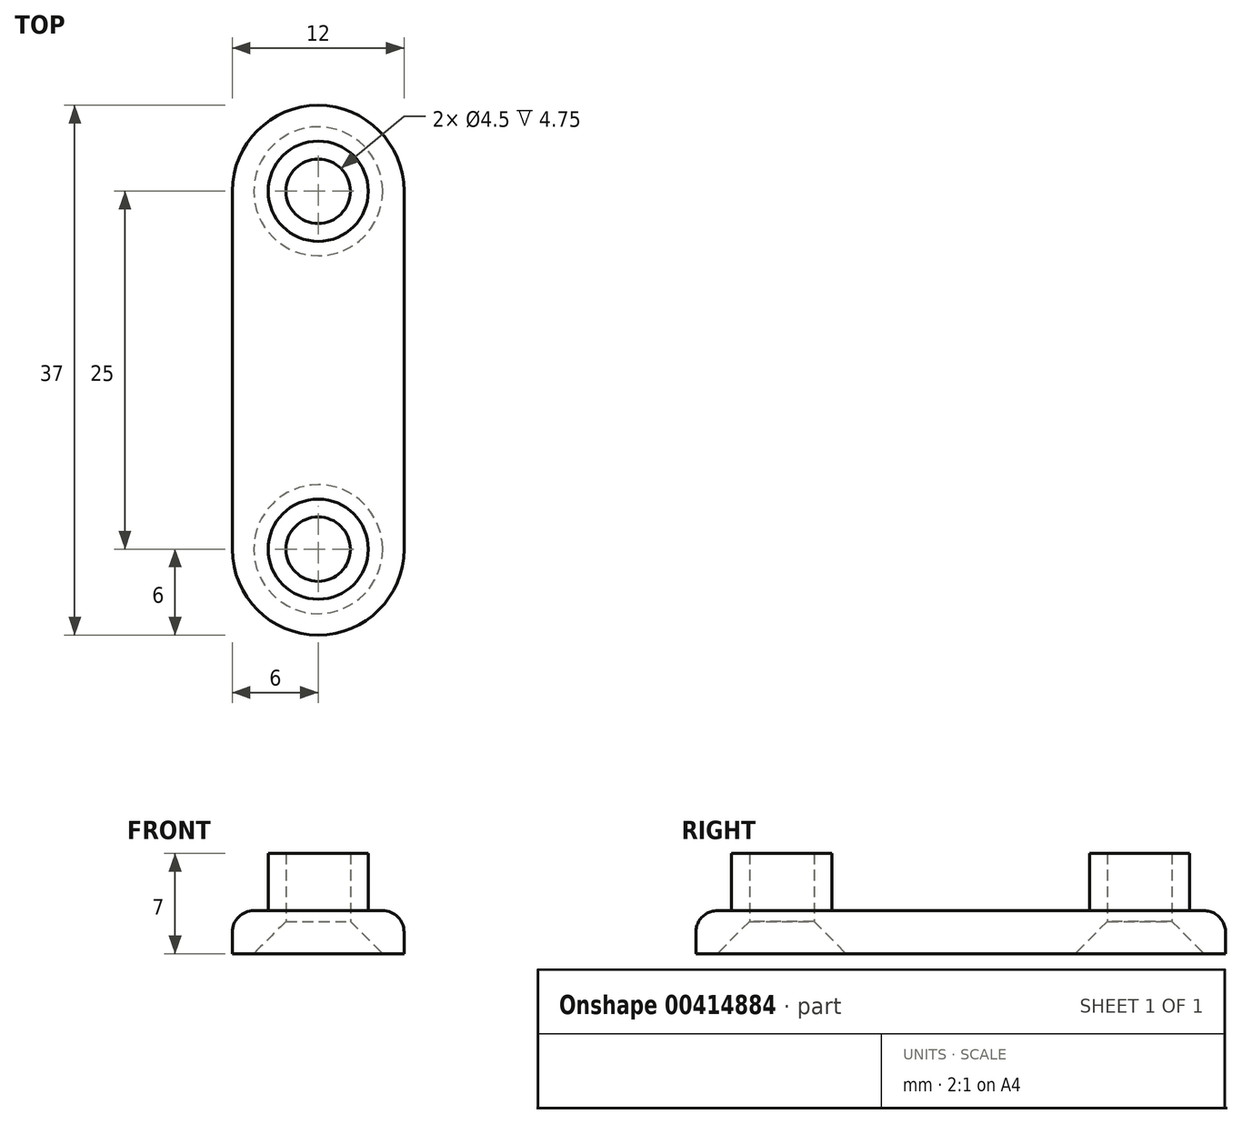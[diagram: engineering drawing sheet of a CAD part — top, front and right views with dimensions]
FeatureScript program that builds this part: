
annotation { "Feature Type Name" : "Feature", "Feature Type Description" : "" }
export const myFeature = defineFeature(function(context is Context, id is Id, definition is map)
    precondition{}
    {
        {
            var Q0;
            Q0=qCreatedBy(makeId("Top.planeOp"),FACE);
            var sketch = newSketch(context, id + "F0", { "sketchPlane" : qUnion([Q0])});
            skLineSegment(sketch, "E0", {"start": v(-6, 12.5) * mm, "end": v(-6, -12.5) * mm});
            skArc(sketch, "E1", {"start": v(-6, 12.5) * mm, "mid": v(0, 18.5) * mm, "end": v(6, 12.5) * mm});
            skArc(sketch, "E2", {"start": v(-6, -12.5) * mm, "mid": v(0, -18.5) * mm, "end": v(6, -12.5) * mm});
            skLineSegment(sketch, "E3", {"start": v(6, 12.5) * mm, "end": v(6, -12.5) * mm});
            skLineSegment(sketch, "E4", {"start": v(0, 12.5) * mm, "end": v(0, -12.5) * mm, "construction": true});
            skSolve(sketch);
        }
        {
            var Q0;
            Q0=makeQuery(id+"F0.imprint","IMPRINT",FACE,{"disambiguationData":[TD([[makeQuery(id+"F0.imprint","IMPRINT",EDGE,{"derivedFrom":sQuery(id+"F0.wireOp",EDGE,"E0")}),1.0]])]});
            extrude(context, id + "F1", {"entities" : qUnion([Q0]), "depth" : 3 * mm});
        }
        {
            var Q0;
            Q0=makeQuery(id+"F1.opExtrude","CAP_FACE",FACE,{"disambiguationData":[OSD([sQuery(id+"F0.wireOp",EDGE,"E0"),sQuery(id+"F0.wireOp",EDGE,"E1"),sQuery(id+"F0.wireOp",EDGE,"E2"),sQuery(id+"F0.wireOp",EDGE,"E3")])],"isStart":false});
            var sketch = newSketch(context, id + "F2", { "sketchPlane" : qUnion([Q0])});
            skArc(sketch, "E5.0", {"start": v(-6, -12.5) * mm, "mid": v(0, -18.5) * mm, "end": v(6, -12.5) * mm});
            skArc(sketch, "E6.0", {"start": v(-6, 12.5) * mm, "mid": v(0, 18.5) * mm, "end": v(6, 12.5) * mm});
            skCircle(sketch, "E7", {"center": v(0, -12.5) * mm, "radius": 3.5 * mm});
            skCircle(sketch, "E8", {"center": v(0, 12.5) * mm, "radius": 3.5 * mm});
            skSolve(sketch);
        }
        {
            var Q0;
            {var subQ0=sQuery(id+"F2.wireOp",EDGE,"OwxIrzHh-1lmq-4VaO-zW4A-XXUzRANfqjct");Q0=makeQuery(id+"F2.imprint","IMPRINT",FACE,{"disambiguationData":[TD([[makeQuery(id+"F2.imprint","IMPRINT",EDGE,{"derivedFrom":subQ0}),-1.0]])]});}
            var Q1;
            {var subQ0=sQuery(id+"F2.wireOp",EDGE,"QkdWbU1v-fYDb-onoO-dhuP-pIeUnw5N6UH5");Q1=makeQuery(id+"F2.imprint","IMPRINT",FACE,{"disambiguationData":[TD([[makeQuery(id+"F2.imprint","IMPRINT",EDGE,{"derivedFrom":subQ0}),1.0]])]});}
            var Q2;
            Q2=makeQuery(id+"F2.imprint","IMPRINT",FACE,{"disambiguationData":[TD([[makeQuery(id+"F2.imprint","IMPRINT",EDGE,{"derivedFrom":sQuery(id+"F2.wireOp",EDGE,"E7")}),1.0]])]});
            var Q3;
            Q3=makeQuery(id+"F2.imprint","IMPRINT",FACE,{"disambiguationData":[TD([[makeQuery(id+"F2.imprint","IMPRINT",EDGE,{"derivedFrom":sQuery(id+"F2.wireOp",EDGE,"E8")}),1.0]])]});
            extrude(context, id + "F3", {"entities" : qUnion([Q0, Q1, Q2, Q3]), "operationType" : NewBodyOperationType.ADD, "depth" : 4 * mm});
        }
        {
            var Q0;
            Q0=makeQuery(id+"F1.opExtrude","CAP_FACE",FACE,{"disambiguationData":[OSD([sQuery(id+"F0.wireOp",EDGE,"E0"),sQuery(id+"F0.wireOp",EDGE,"E1"),sQuery(id+"F0.wireOp",EDGE,"E2"),sQuery(id+"F0.wireOp",EDGE,"E3")])],"isStart":true});
            var sketch = newSketch(context, id + "F4", { "sketchPlane" : qUnion([Q0])});
            skArc(sketch, "E9.0", {"start": v(-6, 12.5) * mm, "mid": v(0, 18.5) * mm, "end": v(6, 12.5) * mm});
            skArc(sketch, "E10.0", {"start": v(-6, -12.5) * mm, "mid": v(0, -18.5) * mm, "end": v(6, -12.5) * mm});
            skSolve(sketch);
        }
        {
            var Q0;
            Q0=sQuery(id+"F4.wireOp",VERTEX,"E9.0.center");
            var Q1;
            Q1=sQuery(id+"F4.wireOp",VERTEX,"E10.0.center");
            var Q2;
            Q2=makeQuery(id+"F1.opExtrude","SWEPT_BODY",BODY,{"disambiguationData":[OSD([sQuery(id+"F0.wireOp",EDGE,"E0"),sQuery(id+"F0.wireOp",EDGE,"E1"),sQuery(id+"F0.wireOp",EDGE,"E2"),sQuery(id+"F0.wireOp",EDGE,"E3")])]});
            hole(context, id + "F5", {"style" : HoleStyle.C_SINK, "endStyle" : HoleEndStyle.THROUGH, "holeDiameter" : 4.5 * mm, "cSinkDiameter" : 9 * mm, "cSinkAngle" : 90 * degree, "isTappedThrough" : true, "tappedDepth" : 12 * mm, "tapClearance" : 3, "locations" : qUnion([Q0, Q1]), "scope" : qUnion([Q2])});
        }
        {
            var Q0;
            Q0=makeQuery(id+"F1.opExtrude","CAP_EDGE",EDGE,{"disambiguationData":[OSD([sQuery(id+"F0.wireOp",EDGE,"E0")])],"isStart":false});
            fillet(context, id + "F6", {"entities" : qUnion([Q0]), "radius" : 1.5 * mm, "tangentPropagation" : true, "allowEdgeOverflow" : false});
        }
    });
